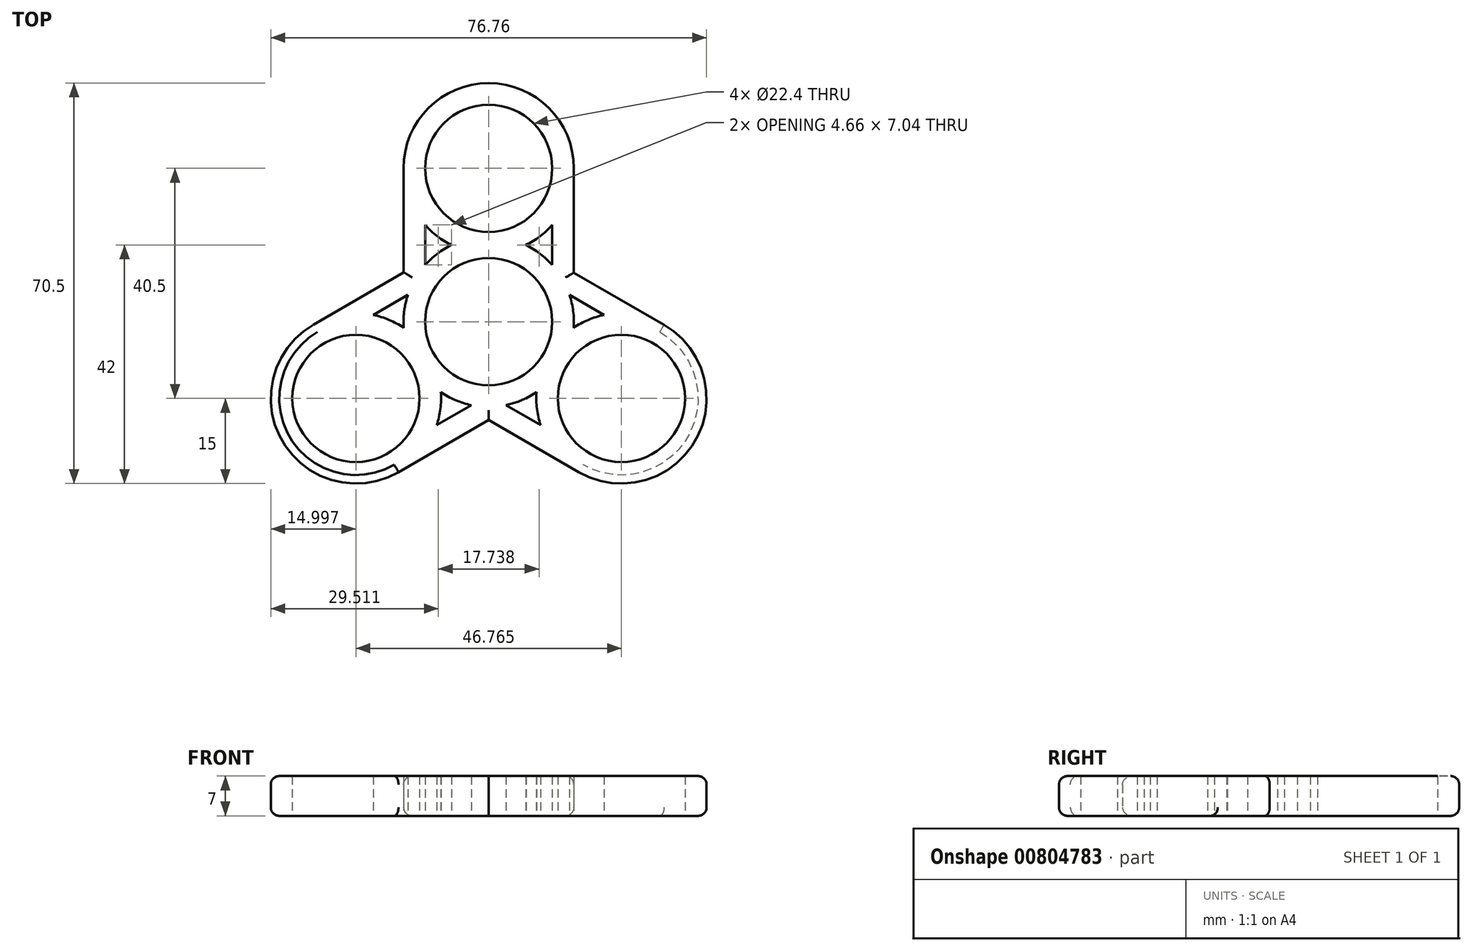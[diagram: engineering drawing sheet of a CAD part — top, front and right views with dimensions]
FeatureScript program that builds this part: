
annotation { "Feature Type Name" : "Feature", "Feature Type Description" : "" }
export const myFeature = defineFeature(function(context is Context, id is Id, definition is map)
    precondition{}
    {
        {
            var Q0;
            Q0=qCreatedBy(makeId("Top.planeOp"),FACE);
            var sketch = newSketch(context, id + "F0", { "sketchPlane" : qUnion([Q0])});
            skCircle(sketch, "E0", {"center": v(0, 0) * mm, "radius": 11.2 * mm});
            skCircle(sketch, "E1", {"center": v(0, 27) * mm, "radius": 11.2 * mm});
            skArc(sketch, "E2", {"start": v(6.54, 13.5) * mm, "mid": v(9.04, 15.03) * mm, "end": v(11.2, 17.02) * mm});
            skArc(sketch, "E3", {"start": v(-6.54, 13.5) * mm, "mid": v(-9.04, 11.97) * mm, "end": v(-11.2, 9.98) * mm});
            skArc(sketch, "E4.1.0", {"start": v(-14.96, -1.09) * mm, "mid": v(-17.54, 0.31) * mm, "end": v(-20.34, 1.19) * mm});
            skCircle(sketch, "E4.1.1", {"center": v(-23.38, -13.5) * mm, "radius": 11.2 * mm});
            skArc(sketch, "E4.2.0", {"start": v(8.42, -12.41) * mm, "mid": v(8.5, -15.35) * mm, "end": v(9.14, -18.21) * mm});
            skCircle(sketch, "E4.2.1", {"center": v(23.38, -13.5) * mm, "radius": 11.2 * mm});
            skArc(sketch, "E5.trimOffspring", {"start": v(-8.42, -12.41) * mm, "mid": v(-5.84, -13.81) * mm, "end": v(-3.04, -14.69) * mm});
            skArc(sketch, "E6.trimOffspring", {"start": v(14.96, -1.09) * mm, "mid": v(14.89, 1.85) * mm, "end": v(14.24, 4.71) * mm});
            skLineSegment(sketch, "E7", {"start": v(11.2, 17.02) * mm, "end": v(11.2, 9.98) * mm});
            skLineSegment(sketch, "E8", {"start": v(15, 27) * mm, "end": v(15, 8.63) * mm});
            skLineSegment(sketch, "E9.1.0", {"start": v(-20.34, 1.19) * mm, "end": v(-14.24, 4.71) * mm});
            skLineSegment(sketch, "E9.1.1", {"start": v(-30.88, -0.5) * mm, "end": v(-14.97, 8.68) * mm});
            skLineSegment(sketch, "E9.2.0", {"start": v(9.14, -18.21) * mm, "end": v(3.04, -14.69) * mm});
            skLineSegment(sketch, "E9.2.1", {"start": v(15.88, -26.5) * mm, "end": v(-0.03, -17.3) * mm});
            skLineSegment(sketch, "E10", {"start": v(-11.2, 17.02) * mm, "end": v(-11.2, 9.98) * mm});
            skLineSegment(sketch, "E11", {"start": v(-15, 27) * mm, "end": v(-14.97, 8.68) * mm});
            skLineSegment(sketch, "E12.1.0", {"start": v(-9.14, -18.21) * mm, "end": v(-3.04, -14.69) * mm});
            skLineSegment(sketch, "E12.1.1", {"start": v(-15.88, -26.5) * mm, "end": v(-0.03, -17.3) * mm});
            skLineSegment(sketch, "E12.2.0", {"start": v(20.34, 1.19) * mm, "end": v(14.24, 4.71) * mm});
            skLineSegment(sketch, "E12.2.1", {"start": v(30.88, -0.5) * mm, "end": v(15, 8.63) * mm});
            skPoint(sketch, "E13.orphan", {"position": v(-11.2, 27) * mm});
            skArc(sketch, "E14.trimOffspring", {"start": v(-11.2, 17.02) * mm, "mid": v(-9.04, 15.03) * mm, "end": v(-6.54, 13.5) * mm});
            skArc(sketch, "E15.trimOffspring", {"start": v(-14.24, 4.71) * mm, "mid": v(-14.89, 1.85) * mm, "end": v(-14.96, -1.09) * mm});
            skLineSegment(sketch, "E16.trimOffspring", {"start": v(-14.96, 1.05) * mm, "end": v(-14.96, -1.09) * mm});
            skArc(sketch, "E17.trimOffspring", {"start": v(-30.88, -0.5) * mm, "mid": v(-36.36, -21.02) * mm, "end": v(-15.85, -26.47) * mm});
            skPoint(sketch, "E18.orphan", {"position": v(-28.98, -3.8) * mm});
            skPoint(sketch, "E19.orphan", {"position": v(11.2, 27) * mm});
            skArc(sketch, "E20.trimOffspring", {"start": v(15, 27) * mm, "mid": v(-0.02, 42) * mm, "end": v(-15, 26.96) * mm});
            skArc(sketch, "E21.trimOffspring", {"start": v(11.2, 9.98) * mm, "mid": v(9.04, 11.97) * mm, "end": v(6.54, 13.5) * mm});
            skArc(sketch, "E22.trimOffspring", {"start": v(20.34, 1.19) * mm, "mid": v(17.54, 0.31) * mm, "end": v(14.96, -1.09) * mm});
            skPoint(sketch, "E23.orphan", {"position": v(28.98, -3.8) * mm});
            skPoint(sketch, "E24.trimOffspring.end.orphan", {"position": v(11.2, 0) * mm});
            skPoint(sketch, "E25.orphan", {"position": v(-17.78, -23.2) * mm});
            skArc(sketch, "E26.trimOffspring", {"start": v(-9.14, -18.21) * mm, "mid": v(-8.5, -15.35) * mm, "end": v(-8.42, -12.41) * mm});
            skLineSegment(sketch, "E27.trimOffspring", {"start": v(6.58, -13.48) * mm, "end": v(8.42, -12.41) * mm});
            skArc(sketch, "E28.trimOffspring", {"start": v(15.88, -26.5) * mm, "mid": v(36.38, -20.98) * mm, "end": v(30.85, -0.49) * mm});
            skPoint(sketch, "E29.orphan", {"position": v(17.78, -23.2) * mm});
            skArc(sketch, "E30.trimOffspring", {"start": v(3.04, -14.69) * mm, "mid": v(5.84, -13.81) * mm, "end": v(8.42, -12.41) * mm});
            skSolve(sketch);
        }
        {
            var Q0;
            Q0=makeQuery(id+"F0.imprint","IMPRINT",FACE,{"disambiguationData":[TD([[makeQuery(id+"F0.imprint","IMPRINT",EDGE,{"derivedFrom":sQuery(id+"F0.wireOp",EDGE,"E0")}),-1.0]])]});
            extrude(context, id + "F1", {"entities" : qUnion([Q0]), "depth" : 7 * mm, "offsetDistance" : 25 * mm});
        }
        {
            var Q0;
            Q0=makeQuery(id+"F1.opExtrude","CAP_EDGE",EDGE,{"disambiguationData":[OSD([sQuery(id+"F0.wireOp",EDGE,"E11")])],"isStart":false});
            var Q1;
            Q1=makeQuery(id+"F1.opExtrude","CAP_EDGE",EDGE,{"disambiguationData":[OSD([sQuery(id+"F0.wireOp",EDGE,"E20.trimOffspring")])],"isStart":false});
            var Q2;
            Q2=makeQuery(id+"F1.opExtrude","CAP_EDGE",EDGE,{"disambiguationData":[OSD([sQuery(id+"F0.wireOp",EDGE,"E8")])],"isStart":false});
            var Q3;
            Q3=makeQuery(id+"F1.opExtrude","CAP_EDGE",EDGE,{"disambiguationData":[OSD([sQuery(id+"F0.wireOp",EDGE,"E12.2.1")])],"isStart":false});
            var Q4;
            Q4=makeQuery(id+"F1.opExtrude","CAP_EDGE",EDGE,{"disambiguationData":[OSD([sQuery(id+"F0.wireOp",EDGE,"E28.trimOffspring")])],"isStart":false});
            var Q5;
            Q5=makeQuery(id+"F1.opExtrude","CAP_EDGE",EDGE,{"disambiguationData":[OSD([sQuery(id+"F0.wireOp",EDGE,"E9.2.1")])],"isStart":false});
            var Q6;
            Q6=makeQuery(id+"F1.opExtrude","CAP_EDGE",EDGE,{"disambiguationData":[OSD([sQuery(id+"F0.wireOp",EDGE,"E12.1.1")])],"isStart":false});
            var Q7;
            Q7=makeQuery(id+"F1.opExtrude","CAP_EDGE",EDGE,{"disambiguationData":[OSD([sQuery(id+"F0.wireOp",EDGE,"E17.trimOffspring")])],"isStart":false});
            var Q8;
            Q8=makeQuery(id+"F1.opExtrude","CAP_EDGE",EDGE,{"disambiguationData":[OSD([sQuery(id+"F0.wireOp",EDGE,"E9.1.1")])],"isStart":false});
            var Q9;
            Q9=makeQuery(id+"F1.opExtrude","CAP_EDGE",EDGE,{"disambiguationData":[OSD([sQuery(id+"F0.wireOp",EDGE,"E8")])],"isStart":true});
            var Q10;
            Q10=makeQuery(id+"F1.opExtrude","CAP_EDGE",EDGE,{"disambiguationData":[OSD([sQuery(id+"F0.wireOp",EDGE,"E20.trimOffspring")])],"isStart":true});
            var Q11;
            Q11=makeQuery(id+"F1.opExtrude","CAP_EDGE",EDGE,{"disambiguationData":[OSD([sQuery(id+"F0.wireOp",EDGE,"E11")])],"isStart":true});
            var Q12;
            Q12=makeQuery(id+"F1.opExtrude","CAP_EDGE",EDGE,{"disambiguationData":[OSD([sQuery(id+"F0.wireOp",EDGE,"E9.1.1")])],"isStart":true});
            var Q13;
            Q13=makeQuery(id+"F1.opExtrude","CAP_EDGE",EDGE,{"disambiguationData":[OSD([sQuery(id+"F0.wireOp",EDGE,"E17.trimOffspring")])],"isStart":true});
            var Q14;
            Q14=makeQuery(id+"F1.opExtrude","CAP_EDGE",EDGE,{"disambiguationData":[OSD([sQuery(id+"F0.wireOp",EDGE,"E12.1.1")])],"isStart":true});
            var Q15;
            Q15=makeQuery(id+"F1.opExtrude","CAP_EDGE",EDGE,{"disambiguationData":[OSD([sQuery(id+"F0.wireOp",EDGE,"E9.2.1")])],"isStart":true});
            var Q16;
            Q16=makeQuery(id+"F1.opExtrude","CAP_EDGE",EDGE,{"disambiguationData":[OSD([sQuery(id+"F0.wireOp",EDGE,"E28.trimOffspring")])],"isStart":true});
            var Q17;
            Q17=makeQuery(id+"F1.opExtrude","CAP_EDGE",EDGE,{"disambiguationData":[OSD([sQuery(id+"F0.wireOp",EDGE,"E12.2.1")])],"isStart":true});
            fillet(context, id + "F2", {"entities" : qUnion([Q0, Q1, Q2, Q3, Q4, Q5, Q6, Q7, Q8, Q9, Q10, Q11, Q12, Q13, Q14, Q15, Q16, Q17]), "radius" : 1.5 * mm, "tangentPropagation" : true, "allowEdgeOverflow" : false});
        }
    });
